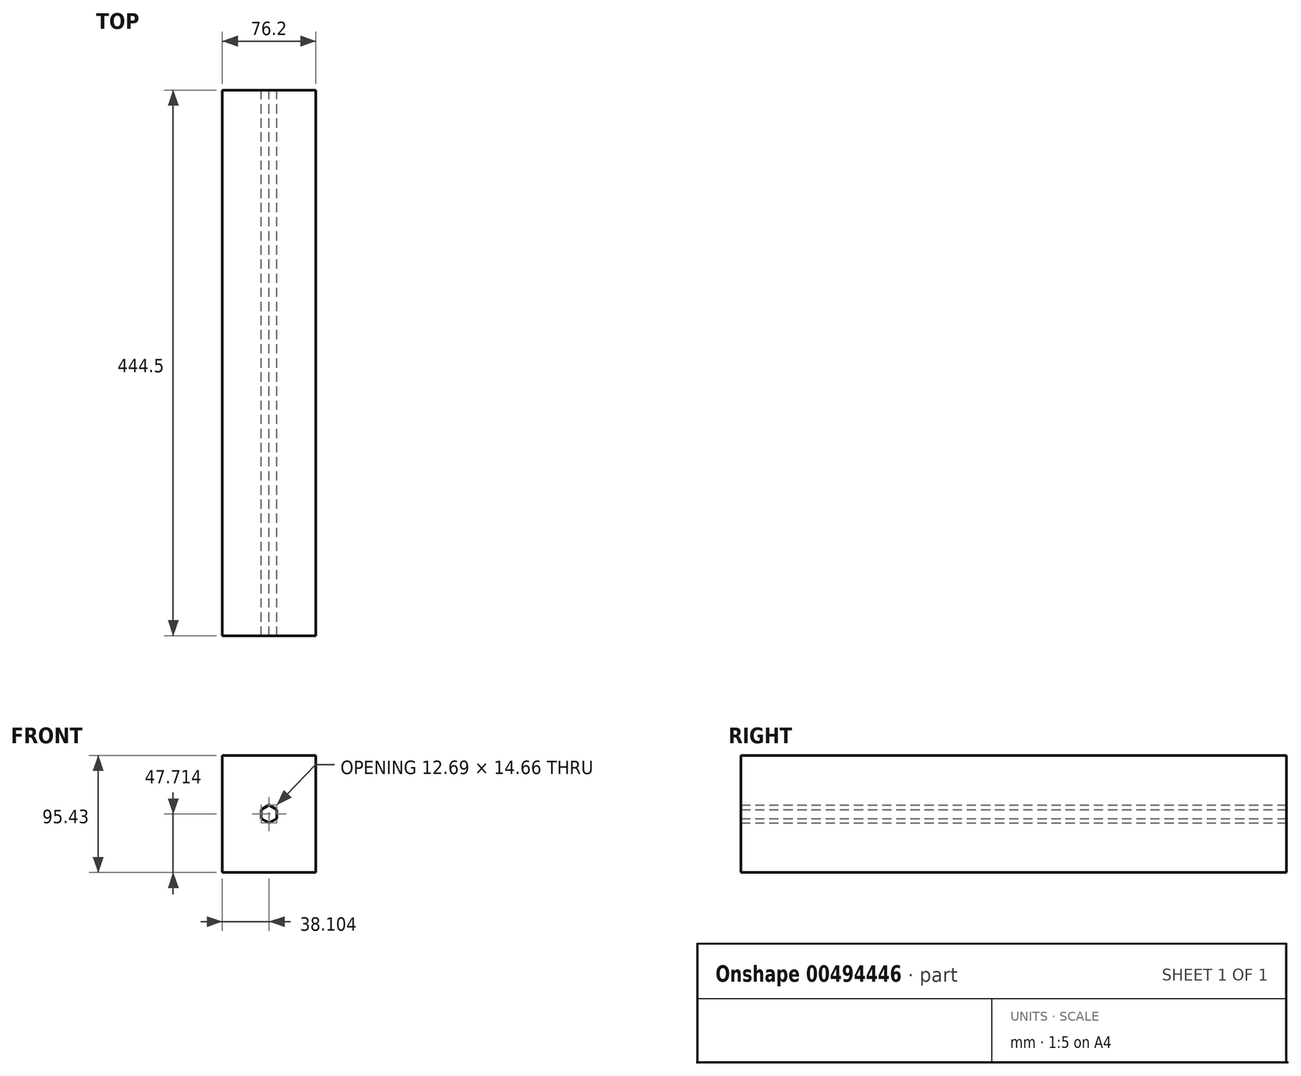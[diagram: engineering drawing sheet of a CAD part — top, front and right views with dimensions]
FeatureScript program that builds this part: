
annotation { "Feature Type Name" : "Feature", "Feature Type Description" : "" }
export const myFeature = defineFeature(function(context is Context, id is Id, definition is map)
    precondition{}
    {
        {
            var Q0;
            Q0=qCreatedBy(makeId("Front.planeOp"),FACE);
            var sketch = newSketch(context, id + "F0", { "sketchPlane" : qUnion([Q0])});
            skCircle(sketch, "E0.cCircle", {"center": v(-130.33, 55.98) * mm, "radius": 7.33 * mm, "construction": true});
            skLineSegment(sketch, "E0.0", {"start": v(-130.33, 48.66) * mm, "end": v(-136.67, 52.32) * mm});
            skLineSegment(sketch, "E0.1", {"start": v(-136.67, 52.32) * mm, "end": v(-136.67, 59.65) * mm});
            skLineSegment(sketch, "E0.2", {"start": v(-136.67, 59.65) * mm, "end": v(-130.33, 63.31) * mm});
            skLineSegment(sketch, "E0.3", {"start": v(-130.33, 63.31) * mm, "end": v(-123.98, 59.65) * mm});
            skLineSegment(sketch, "E0.4", {"start": v(-123.98, 59.65) * mm, "end": v(-123.98, 52.32) * mm});
            skLineSegment(sketch, "E0.5", {"start": v(-123.98, 52.32) * mm, "end": v(-130.33, 48.66) * mm});
            skLineSegment(sketch, "E1", {"start": v(-130.33, 63.31) * mm, "end": v(-130.33, 103.7) * mm});
            skLineSegment(sketch, "E2", {"start": v(-130.33, 48.66) * mm, "end": v(-130.33, 8.27) * mm});
            skLineSegment(sketch, "E3", {"start": v(-130.33, 103.7) * mm, "end": v(-92.23, 103.7) * mm});
            skLineSegment(sketch, "E4", {"start": v(-130.33, 8.27) * mm, "end": v(-92.23, 8.27) * mm});
            skLineSegment(sketch, "E5", {"start": v(-92.23, 103.7) * mm, "end": v(-92.23, 8.27) * mm});
            skLineSegment(sketch, "E6", {"start": v(-130.33, 103.7) * mm, "end": v(-168.43, 103.7) * mm});
            skLineSegment(sketch, "E7", {"start": v(-130.33, 8.27) * mm, "end": v(-168.43, 8.27) * mm});
            skLineSegment(sketch, "E8", {"start": v(-168.43, 103.7) * mm, "end": v(-168.43, 8.27) * mm});
            skSolve(sketch);
        }
        {
            var Q0;
            Q0 = qSketchRegion(id + "F0", true);
            extrude(context, id + "F1", {"entities" : qUnion([Q0]), "depth" : 444.5 * mm});
        }
    });
